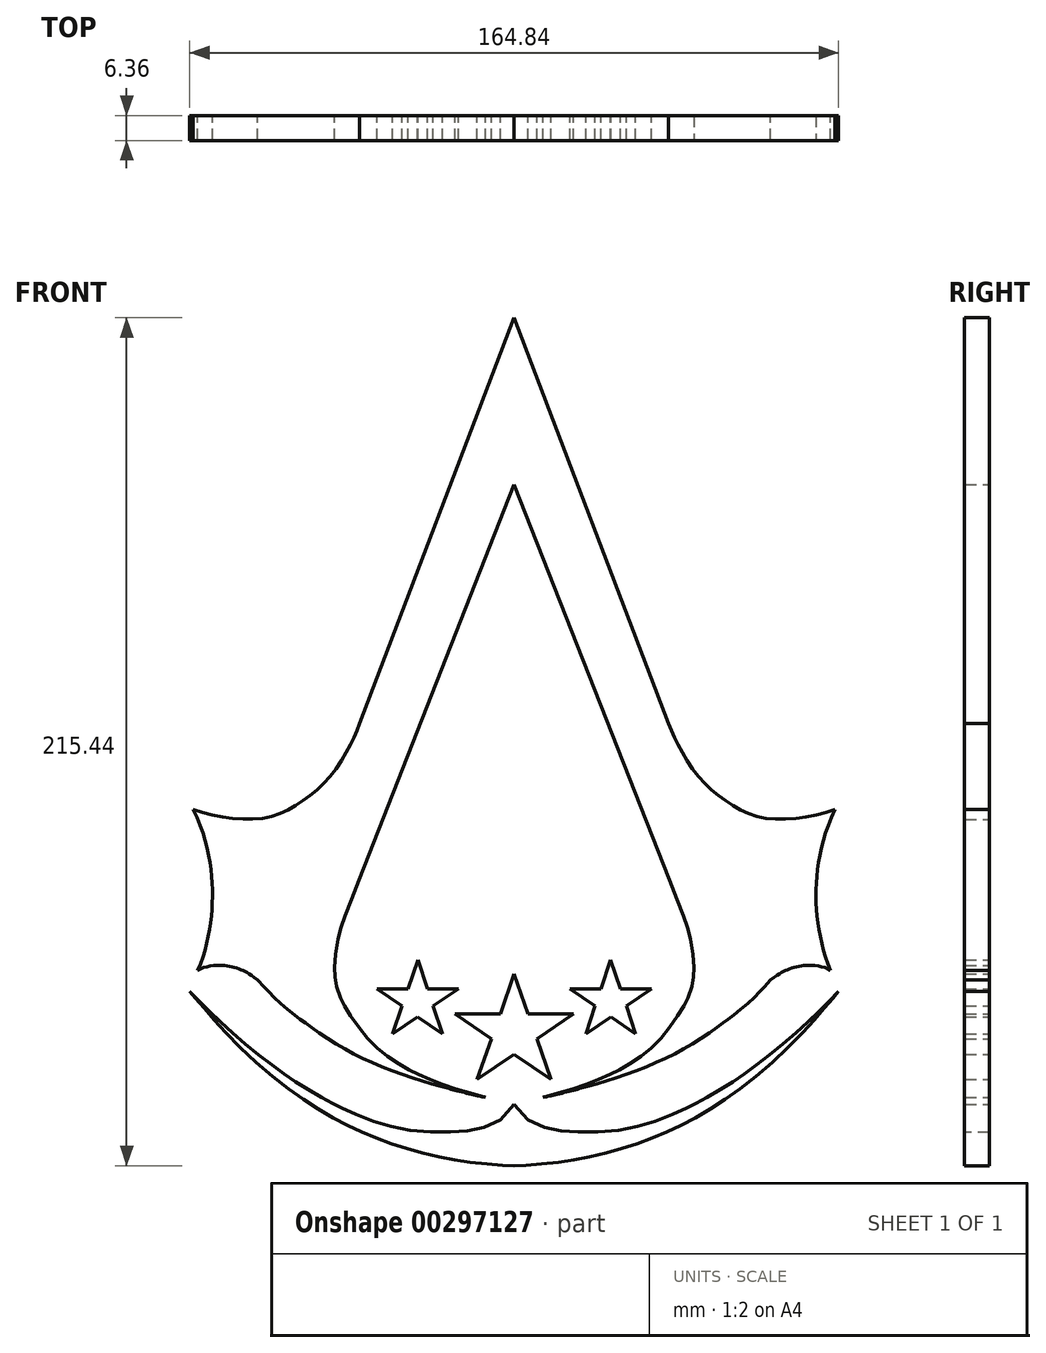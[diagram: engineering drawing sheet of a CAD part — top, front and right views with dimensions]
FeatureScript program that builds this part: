
annotation { "Feature Type Name" : "Feature", "Feature Type Description" : "" }
export const myFeature = defineFeature(function(context is Context, id is Id, definition is map)
    precondition{}
    {
        {
            var Q0;
            Q0=qCreatedBy(makeId("Front.planeOp"),FACE);
            var sketch = newSketch(context, id + "F0", { "sketchPlane" : qUnion([Q0])});
            skLineSegment(sketch, "E0", {"start": v(0.74, 78.09) * mm, "end": v(-38.5, -25.03) * mm});
            skFitSpline(sketch, "E1", {"points": [v(-38.5, -25.03) * mm, v(-41.14, -30.86) * mm, v(-46.47, -38.94) * mm, v(-52.94, -44.63) * mm, v(-60.34, -48.46) * mm, v(-70.18, -49.18) * mm, v(-80.8, -46.9) * mm], "startDerivative": vector(-16.34, -39.3) * mm, "endDerivative": vector(-50.47, 18.6) * mm});
            skFitSpline(sketch, "E2", {"points": [v(-80.8, -46.9) * mm, v(-76.27, -62.66) * mm, v(-76.3, -74.7) * mm, v(-79.65, -87.77) * mm], "startDerivative": vector(23.22, -46.7) * mm, "endDerivative": vector(-16.73, -38.92) * mm});
            skFitSpline(sketch, "E3", {"points": [v(-79.65, -87.77) * mm, v(-74.34, -86.45) * mm, v(-71, -86.8) * mm, v(-68.16, -87.77) * mm, v(-64.41, -90.2) * mm], "startDerivative": vector(15.4, 10.91) * mm, "endDerivative": vector(23, -17.55) * mm});
            skFitSpline(sketch, "E4", {"points": [v(-64.41, -90.2) * mm, v(-60.62, -94.27) * mm, v(-55, -99.06) * mm, v(-51.56, -101.65) * mm, v(-44.72, -106.3) * mm, v(-36.46, -110.67) * mm, v(-26.64, -114.51) * mm, v(-17.85, -117.24) * mm], "startDerivative": vector(47.56, -46.99) * mm, "endDerivative": vector(55.55, -15.16) * mm});
            skFitSpline(sketch, "E5", {"points": [v(-17.85, -117.24) * mm, v(-13.47, -118.4) * mm, v(-8.33, -119.62) * mm, v(-6.52, -119.99) * mm], "startDerivative": vector(11.18, -3.06) * mm, "endDerivative": vector(6.57, -1.25) * mm});
            skFitSpline(sketch, "E6", {"points": [v(-6.52, -119.99) * mm, v(-13.72, -117.93) * mm, v(-19.07, -116.12) * mm, v(-23.78, -114.1) * mm, v(-26.72, -112.58) * mm, v(-31.15, -109.84) * mm, v(-35.37, -106.21) * mm, v(-39.04, -101.87) * mm, v(-42.01, -97.34) * mm, v(-43.23, -95.24) * mm, v(-44.5, -91.26) * mm, v(-44.85, -88.71) * mm, v(-44.85, -85.22) * mm, v(-43.8, -78.48) * mm, v(-42.57, -74.72) * mm, v(-38.67, -64.72) * mm], "startDerivative": vector(-94.63, 23.57) * mm, "endDerivative": vector(46.01, 117.17) * mm});
            skLineSegment(sketch, "E7", {"start": v(-38.67, -64.72) * mm, "end": v(0.73, 35.68) * mm});
            skLineSegment(sketch, "E8.MirrorCS", {"start": v(40.14, -64.72) * mm, "end": v(0.73, 35.68) * mm});
            skLineSegment(sketch, "E9.MirrorCS", {"start": v(0.74, 78.09) * mm, "end": v(39.97, -25.03) * mm});
            skFitSpline(sketch, "E10.MirrorCS", {"points": [v(39.97, -25.03) * mm, v(42.62, -30.86) * mm, v(47.95, -38.94) * mm, v(54.42, -44.63) * mm, v(61.82, -48.46) * mm, v(71.65, -49.18) * mm, v(82.27, -46.9) * mm], "startDerivative": vector(16.34, -39.3) * mm, "endDerivative": vector(50.47, 18.6) * mm});
            skFitSpline(sketch, "E11.MirrorCS", {"points": [v(82.27, -46.9) * mm, v(77.75, -62.66) * mm, v(77.77, -74.7) * mm, v(81.13, -87.77) * mm], "startDerivative": vector(-23.22, -46.7) * mm, "endDerivative": vector(16.73, -38.92) * mm});
            skFitSpline(sketch, "E12.MirrorCS", {"points": [v(65.89, -90.2) * mm, v(62.1, -94.27) * mm, v(56.48, -99.06) * mm, v(53.04, -101.65) * mm, v(46.2, -106.3) * mm, v(37.93, -110.67) * mm, v(28.12, -114.51) * mm, v(19.32, -117.24) * mm], "startDerivative": vector(-47.56, -46.99) * mm, "endDerivative": vector(-55.55, -15.16) * mm});
            skFitSpline(sketch, "E13.MirrorCS", {"points": [v(81.13, -87.77) * mm, v(75.82, -86.45) * mm, v(72.48, -86.8) * mm, v(69.63, -87.77) * mm, v(65.89, -90.2) * mm], "startDerivative": vector(-15.4, 10.91) * mm, "endDerivative": vector(-23, -17.55) * mm});
            skFitSpline(sketch, "E14.MirrorCS", {"points": [v(19.32, -117.24) * mm, v(14.95, -118.4) * mm, v(9.8, -119.62) * mm, v(8, -119.99) * mm], "startDerivative": vector(-11.18, -3.06) * mm, "endDerivative": vector(-6.57, -1.25) * mm});
            skFitSpline(sketch, "E15.MirrorCS", {"points": [v(8, -119.99) * mm, v(15.2, -117.93) * mm, v(20.55, -116.12) * mm, v(25.25, -114.1) * mm, v(28.2, -112.58) * mm, v(32.63, -109.84) * mm, v(36.84, -106.21) * mm, v(40.52, -101.87) * mm, v(43.49, -97.34) * mm, v(44.71, -95.24) * mm, v(45.98, -91.26) * mm, v(46.32, -88.71) * mm, v(46.32, -85.22) * mm, v(45.27, -78.48) * mm, v(44.05, -74.72) * mm, v(40.14, -64.72) * mm], "startDerivative": vector(94.63, 23.57) * mm, "endDerivative": vector(-46.01, 117.17) * mm});
            skLineSegment(sketch, "E16", {"start": v(-26.24, -92.39) * mm, "end": v(-34.1, -92.39) * mm});
            skLineSegment(sketch, "E17", {"start": v(-34.1, -92.39) * mm, "end": v(-27.77, -96.76) * mm});
            skLineSegment(sketch, "E18", {"start": v(-27.77, -96.76) * mm, "end": v(-30.13, -103.86) * mm});
            skLineSegment(sketch, "E19", {"start": v(-30.13, -103.86) * mm, "end": v(-23.84, -99.53) * mm});
            skLineSegment(sketch, "E20", {"start": v(-23.84, -99.53) * mm, "end": v(-17.46, -103.9) * mm});
            skLineSegment(sketch, "E21", {"start": v(-17.46, -103.9) * mm, "end": v(-19.83, -96.76) * mm});
            skLineSegment(sketch, "E22", {"start": v(-19.83, -96.76) * mm, "end": v(-13.43, -92.39) * mm});
            skLineSegment(sketch, "E23", {"start": v(-13.43, -92.39) * mm, "end": v(-21.33, -92.39) * mm});
            skLineSegment(sketch, "E24", {"start": v(-21.33, -92.39) * mm, "end": v(-23.76, -85.09) * mm});
            skLineSegment(sketch, "E25", {"start": v(-23.76, -85.09) * mm, "end": v(-26.24, -92.39) * mm});
            skLineSegment(sketch, "E26", {"start": v(0.74, -88.6) * mm, "end": v(-2.76, -98.74) * mm});
            skLineSegment(sketch, "E27", {"start": v(-2.76, -98.74) * mm, "end": v(-14.35, -98.74) * mm});
            skLineSegment(sketch, "E28", {"start": v(-14.35, -98.74) * mm, "end": v(-5, -105.08) * mm});
            skLineSegment(sketch, "E29", {"start": v(-5, -105.08) * mm, "end": v(-8.66, -115.42) * mm});
            skLineSegment(sketch, "E30", {"start": v(-8.66, -115.42) * mm, "end": v(0.74, -109.14) * mm});
            skLineSegment(sketch, "E31.MirrorCS", {"start": v(0.74, -88.6) * mm, "end": v(4.23, -98.74) * mm});
            skLineSegment(sketch, "E32.MirrorCS", {"start": v(4.23, -98.74) * mm, "end": v(15.83, -98.74) * mm});
            skLineSegment(sketch, "E33.MirrorCS", {"start": v(15.83, -98.74) * mm, "end": v(6.48, -105.08) * mm});
            skLineSegment(sketch, "E34.MirrorCS", {"start": v(6.48, -105.08) * mm, "end": v(10.14, -115.42) * mm});
            skLineSegment(sketch, "E35.MirrorCS", {"start": v(10.14, -115.42) * mm, "end": v(0.74, -109.14) * mm});
            skLineSegment(sketch, "E36.MirrorCS", {"start": v(25.32, -99.53) * mm, "end": v(18.93, -103.9) * mm});
            skLineSegment(sketch, "E37.MirrorCS", {"start": v(18.93, -103.9) * mm, "end": v(21.3, -96.76) * mm});
            skLineSegment(sketch, "E38.MirrorCS", {"start": v(35.57, -92.39) * mm, "end": v(29.24, -96.76) * mm});
            skLineSegment(sketch, "E39.MirrorCS", {"start": v(21.3, -96.76) * mm, "end": v(14.9, -92.39) * mm});
            skLineSegment(sketch, "E40.MirrorCS", {"start": v(29.24, -96.76) * mm, "end": v(31.6, -103.86) * mm});
            skLineSegment(sketch, "E41.MirrorCS", {"start": v(22.8, -92.39) * mm, "end": v(25.23, -85.09) * mm});
            skLineSegment(sketch, "E42.MirrorCS", {"start": v(14.9, -92.39) * mm, "end": v(22.8, -92.39) * mm});
            skLineSegment(sketch, "E43.MirrorCS", {"start": v(27.71, -92.39) * mm, "end": v(35.57, -92.39) * mm});
            skLineSegment(sketch, "E44.MirrorCS", {"start": v(25.23, -85.09) * mm, "end": v(27.71, -92.39) * mm});
            skLineSegment(sketch, "E45.MirrorCS", {"start": v(31.6, -103.86) * mm, "end": v(25.32, -99.53) * mm});
            skFitSpline(sketch, "E46", {"points": [v(0.74, -121.8) * mm, v(-7.3, -127.67) * mm, v(-15.22, -128.81) * mm, v(-26.74, -128.2) * mm, v(-36.19, -125.64) * mm, v(-43.47, -122.56) * mm, v(-45.87, -121.32) * mm, v(-51.13, -118.34) * mm, v(-56.07, -115.16) * mm, v(-61.01, -111.64) * mm, v(-67.38, -106.62) * mm, v(-73.3, -101.38) * mm, v(-78.11, -96.73) * mm, v(-81.68, -93.06) * mm], "startDerivative": vector(-60.76, -123.02) * mm, "endDerivative": vector(-52.45, 54.6) * mm});
            skFitSpline(sketch, "E47", {"points": [v(-81.68, -93.06) * mm, v(-80.35, -94.71) * mm, v(-77.44, -98.05) * mm, v(-72.49, -103.57) * mm, v(-64.2, -111.72) * mm, v(-55.49, -118.67) * mm, v(-48.75, -123.13) * mm, v(-42.22, -126.8) * mm, v(-36.6, -129.44) * mm, v(-30.19, -131.85) * mm, v(-23.92, -133.8) * mm, v(-16.52, -135.47) * mm, v(-10.35, -136.48) * mm, v(-3.08, -137.2) * mm, v(0.74, -137.35) * mm], "startDerivative": vector(29.65, -38.18) * mm, "endDerivative": vector(63.96, -1.34) * mm});
            skFitSpline(sketch, "E48.MirrorCS", {"points": [v(8, -119.99) * mm, v(15.2, -117.93) * mm, v(20.55, -116.12) * mm, v(25.25, -114.1) * mm, v(28.2, -112.58) * mm, v(32.63, -109.84) * mm, v(36.84, -106.21) * mm, v(40.52, -101.87) * mm, v(43.49, -97.34) * mm, v(44.71, -95.24) * mm, v(45.98, -91.26) * mm, v(46.32, -88.71) * mm, v(46.32, -85.22) * mm, v(45.27, -78.48) * mm, v(44.05, -74.72) * mm, v(40.14, -64.72) * mm], "startDerivative": vector(94.63, 23.57) * mm, "endDerivative": vector(-46.01, 117.17) * mm});
            skFitSpline(sketch, "E49.MirrorCS", {"points": [v(0.74, -121.8) * mm, v(8.78, -127.67) * mm, v(16.7, -128.81) * mm, v(28.22, -128.2) * mm, v(37.67, -125.64) * mm, v(44.94, -122.56) * mm, v(47.35, -121.32) * mm, v(52.6, -118.34) * mm, v(57.54, -115.16) * mm, v(62.49, -111.64) * mm, v(68.85, -106.62) * mm, v(74.79, -101.38) * mm, v(79.59, -96.73) * mm, v(83.16, -93.06) * mm], "startDerivative": vector(60.76, -123.02) * mm, "endDerivative": vector(52.45, 54.6) * mm});
            skFitSpline(sketch, "E50.MirrorCS", {"points": [v(83.16, -93.06) * mm, v(81.83, -94.71) * mm, v(78.92, -98.05) * mm, v(73.97, -103.57) * mm, v(65.67, -111.72) * mm, v(56.96, -118.67) * mm, v(50.22, -123.13) * mm, v(43.7, -126.8) * mm, v(38.08, -129.44) * mm, v(31.66, -131.85) * mm, v(25.4, -133.8) * mm, v(18, -135.47) * mm, v(11.82, -136.48) * mm, v(4.55, -137.2) * mm, v(0.74, -137.35) * mm], "startDerivative": vector(-29.65, -38.18) * mm, "endDerivative": vector(-63.96, -1.34) * mm});
            skSolve(sketch);
        }
        {
            var Q0;
            Q0 = qSketchRegion(id + "F0", true);
            extrude(context, id + "F1", {"entities" : qUnion([Q0]), "endBound" : BoundingType.SYMMETRIC, "depth" : 6.35 * mm});
        }
    });
